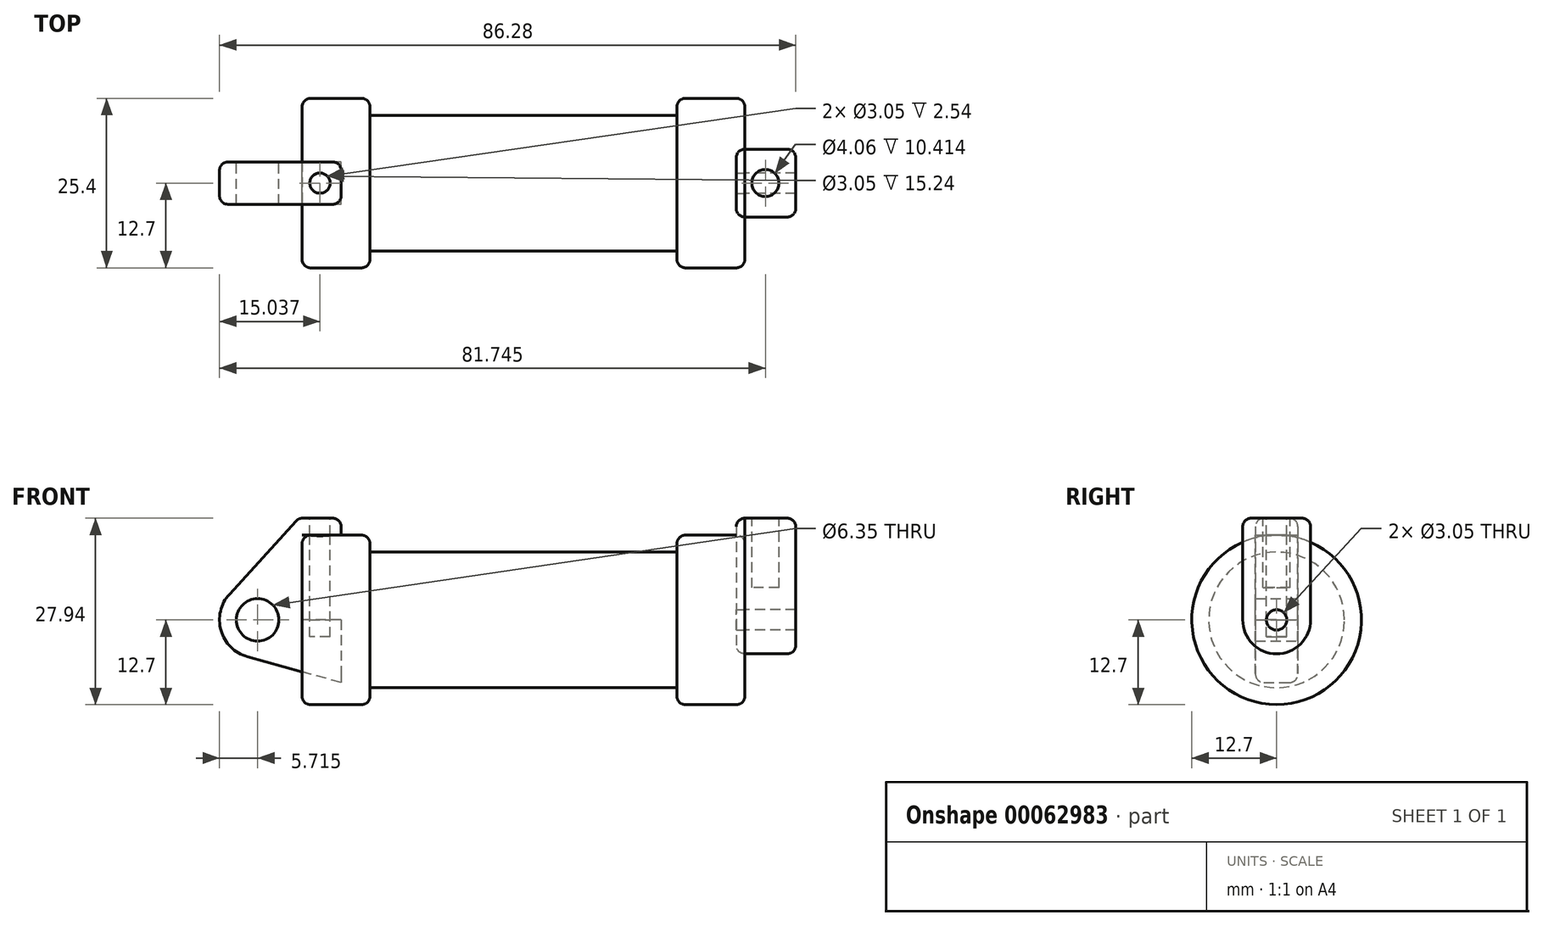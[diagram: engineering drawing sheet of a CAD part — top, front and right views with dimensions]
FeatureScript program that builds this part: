
annotation { "Feature Type Name" : "Feature", "Feature Type Description" : "" }
export const myFeature = defineFeature(function(context is Context, id is Id, definition is map)
    precondition{}
    {
        {
            var Q0;
            Q0=qCreatedBy(makeId("Front.planeOp"),FACE);
            var sketch = newSketch(context, id + "F0", { "sketchPlane" : qUnion([Q0])});
            skLineSegment(sketch, "E0", {"start": v(0, 0) * mm, "end": v(0, 12.7) * mm});
            skLineSegment(sketch, "E1", {"start": v(0, 12.7) * mm, "end": v(10.16, 12.7) * mm});
            skLineSegment(sketch, "E2", {"start": v(10.16, 12.7) * mm, "end": v(10.16, 10.16) * mm});
            skLineSegment(sketch, "E3", {"start": v(10.16, 10.16) * mm, "end": v(56.13, 10.16) * mm});
            skLineSegment(sketch, "E4", {"start": v(56.13, 10.16) * mm, "end": v(56.13, 12.7) * mm});
            skLineSegment(sketch, "E5", {"start": v(56.13, 12.7) * mm, "end": v(66.3, 12.7) * mm});
            skLineSegment(sketch, "E6", {"start": v(66.3, 12.7) * mm, "end": v(66.3, 0) * mm});
            skLineSegment(sketch, "E7", {"start": v(66.3, 0) * mm, "end": v(0, 0) * mm});
            skLineSegment(sketch, "E8", {"start": v(5.84, 15.24) * mm, "end": v(-0.5, 15.24) * mm});
            skLineSegment(sketch, "E9", {"start": v(-0.5, 15.24) * mm, "end": v(-10.88, 3.85) * mm});
            skLineSegment(sketch, "E10", {"start": v(0, 0) * mm, "end": v(-6.65, 0) * mm});
            skCircle(sketch, "E11", {"center": v(-6.65, 0) * mm, "radius": 5.72 * mm});
            skCircle(sketch, "E12", {"center": v(-6.65, 0) * mm, "radius": 3.18 * mm});
            skLineSegment(sketch, "E13", {"start": v(5.84, 15.24) * mm, "end": v(5.84, -9.4) * mm});
            skLineSegment(sketch, "E14", {"start": v(5.84, -9.4) * mm, "end": v(-8.18, -5.5) * mm});
            skSolve(sketch);
        }
        {
            var Q0;
            {var subQ0=sQuery(id+"F0.wireOp",EDGE,"E0");Q0=makeQuery(id+"F0.imprint","IMPRINT",FACE,{"disambiguationData":[TD([[makeQuery(id+"F0.imprint","IMPRINT",EDGE,{"derivedFrom":subQ0}),-1.0]])]});}
            var Q1;
            {var subQ0=sQuery(id+"F0.wireOp",EDGE,"E2");Q1=makeQuery(id+"F0.imprint","IMPRINT",FACE,{"disambiguationData":[TD([[makeQuery(id+"F0.imprint","IMPRINT",EDGE,{"derivedFrom":subQ0}),-1.0]])]});}
            var Q2;
            Q2=sQuery(id+"F0.wireOp",EDGE,"E7");
            revolve(context, id + "F1", {"entities" : qUnion([Q0, Q1]), "axis" : qUnion([Q2]), "revolveType" : RevolveType.FULL});
        }
        {
            var Q0;
            {var subQ3=sQuery(id+"F0.wireOp",EDGE,"E0");Q0=makeQuery(id+"F0.imprint","IMPRINT",FACE,{"disambiguationData":[TD([[makeQuery(id+"F0.imprint","IMPRINT",EDGE,{"derivedFrom":subQ3}),1.0]])]});}
            var Q1;
            {var subQ4=sQuery(id+"F0.wireOp",EDGE,"E12");Q1=makeQuery(id+"F0.imprint","IMPRINT",FACE,{"disambiguationData":[TD([[makeQuery(id+"F0.imprint","IMPRINT",EDGE,{"derivedFrom":subQ4}),-1.0]])]});}
            var Q2;
            {var subQ0=sQuery(id+"F0.wireOp",EDGE,"E14");Q2=makeQuery(id+"F0.imprint","IMPRINT",FACE,{"disambiguationData":[TD([[makeQuery(id+"F0.imprint","IMPRINT",EDGE,{"derivedFrom":subQ0}),-1.0]])]});}
            extrude(context, id + "F2", {"entities" : qUnion([Q0, Q1, Q2]), "endBound" : BoundingType.SYMMETRIC, "depth" : 6.35 * mm});
        }
        {
            var Q0;
            Q0=makeQuery(id+"F1.opRevolve","SWEPT_FACE",FACE,{"disambiguationData":[OSD([sQuery(id+"F0.wireOp",EDGE,"E6")])]});
            var sketch = newSketch(context, id + "F3", { "sketchPlane" : qUnion([Q0])});
            skCircle(sketch, "E15", {"center": v(0, 0) * mm, "radius": 1.52 * mm});
            skCircle(sketch, "E16", {"center": v(0, 0) * mm, "radius": 5.08 * mm});
            skLineSegment(sketch, "E17", {"start": v(-5.08, 0) * mm, "end": v(-5.08, 15.24) * mm});
            skLineSegment(sketch, "E18", {"start": v(-5.08, 15.24) * mm, "end": v(5.08, 15.24) * mm});
            skLineSegment(sketch, "E19", {"start": v(5.08, 15.24) * mm, "end": v(5.08, 0) * mm});
            skSolve(sketch);
        }
        {
            var Q0;
            {var subQ0=sQuery(id+"F3.wireOp",EDGE,"E18");Q0=makeQuery(id+"F3.imprint","IMPRINT",FACE,{"disambiguationData":[TD([[makeQuery(id+"F3.imprint","IMPRINT",EDGE,{"derivedFrom":subQ0}),-1.0]])]});}
            var Q1;
            {var subQ0=sQuery(id+"F3.wireOp",EDGE,"E17");var subQ1=sQuery(id+"F3.wireOp",EDGE,"E16");var subQ2=makeQuery(id+"F3.imprint","INTERSECT",VERTEX,{"derivedFrom":[subQ1,subQ0]});Q1=makeQuery(id+"F3.imprint","IMPRINT",FACE,{"disambiguationData":[TD([[makeQuery(id+"F3.imprint","IMPRINT",EDGE,{"disambiguationData":[TD([[subQ2,1.0]])],"derivedFrom":subQ1}),-1.0]])]});}
            var Q2;
            Q2=makeQuery(id+"F3.imprint","IMPRINT",FACE,{"disambiguationData":[TD([[makeQuery(id+"F3.imprint","IMPRINT",EDGE,{"derivedFrom":sQuery(id+"F3.wireOp",EDGE,"E15")}),-1.0]])]});
            extrude(context, id + "F4", {"entities" : qUnion([Q0, Q1, Q2]), "depth" : 7.62 * mm});
        }
        {
            var Q0;
            Q0 = qSketchRegion(id + "F3", true);
            extrude(context, id + "F5", {"entities" : qUnion([Q0]), "oppositeDirection" : true, "depth" : 1.27 * mm});
        }
        {
            var Q0;
            Q0=makeQuery(id+"F2.opExtrude","SWEPT_FACE",FACE,{"disambiguationData":[OSD([sQuery(id+"F0.wireOp",EDGE,"E8")])]});
            var sketch = newSketch(context, id + "F6", { "sketchPlane" : qUnion([Q0])});
            skCircle(sketch, "E20", {"center": v(2.67, 0) * mm, "radius": 1.52 * mm});
            skSolve(sketch);
        }
        {
            var Q0;
            Q0=makeQuery(id+"F6.imprint","IMPRINT",FACE,{"disambiguationData":[TD([[makeQuery(id+"F6.imprint","IMPRINT",EDGE,{"derivedFrom":sQuery(id+"F6.wireOp",EDGE,"E20")}),1.0]])]});
            extrude(context, id + "F7", {"entities" : qUnion([Q0]), "operationType" : NewBodyOperationType.REMOVE, "oppositeDirection" : true, "depth" : 17.78 * mm});
        }
        {
            var Q0;
            Q0=makeQuery(id+"F4.opExtrude","SWEPT_FACE",FACE,{"disambiguationData":[OSD([sQuery(id+"F3.wireOp",EDGE,"E18")])]});
            var sketch = newSketch(context, id + "F8", { "sketchPlane" : qUnion([Q0])});
            skCircle(sketch, "E21", {"center": v(69.38, 0) * mm, "radius": 2.03 * mm});
            skLineSegment(sketch, "E22", {"start": v(64.84, 0) * mm, "end": v(73.91, 0) * mm, "construction": true});
            skLineSegment(sketch, "E23", {"start": v(69.38, 5.08) * mm, "end": v(69.38, -5.08) * mm, "construction": true});
            skSolve(sketch);
        }
        {
            var Q0;
            Q0=makeQuery(id+"F8.imprint","IMPRINT",FACE,{"disambiguationData":[TD([[makeQuery(id+"F8.imprint","IMPRINT",EDGE,{"derivedFrom":sQuery(id+"F8.wireOp",EDGE,"E21")}),1.0]])]});
            var Q1;
            Q1=sQuery(id+"F8.wireOp",EDGE,"E21");
            extrude(context, id + "F9", {"entities" : qUnion([Q0]), "operationType" : NewBodyOperationType.REMOVE, "surfaceEntities" : qUnion([Q1]), "oppositeDirection" : true, "depth" : 10.4 * mm});
        }
        {
            var Q0;
            Q0=makeQuery(id+"F4.opExtrude","CAP_EDGE",EDGE,{"disambiguationData":[OSD([sQuery(id+"F3.wireOp",EDGE,"E18")])],"isStart":false});
            var Q1;
            Q1=makeQuery(id+"F4.opExtrude","SWEPT_EDGE",EDGE,{"disambiguationData":[OSD([sQuery(id+"F3.wireOp",EDGE,"E17"),sQuery(id+"F3.wireOp",EDGE,"E18")])]});
            var Q2;
            Q2=makeQuery(id+"F4.opExtrude","SWEPT_EDGE",EDGE,{"disambiguationData":[OSD([sQuery(id+"F3.wireOp",EDGE,"E18"),sQuery(id+"F3.wireOp",EDGE,"E19")])]});
            var Q3;
            Q3=makeQuery(id+"F4.opExtrude","CAP_EDGE",EDGE,{"disambiguationData":[OSD([sQuery(id+"F3.wireOp",EDGE,"E17")])],"isStart":false});
            var Q4;
            Q4=makeQuery(id+"F4.opExtrude","CAP_EDGE",EDGE,{"disambiguationData":[OSD([sQuery(id+"F3.wireOp",EDGE,"E19")])],"isStart":false});
            var Q5;
            Q5=makeQuery(id+"F4.opExtrude","CAP_EDGE",EDGE,{"disambiguationData":[OSD([sQuery(id+"F3.wireOp",EDGE,"E16")])],"isStart":false});
            var Q6;
            Q6=makeQuery(id+"F1.opRevolve","SWEPT_EDGE",EDGE,{"disambiguationData":[OSD([sQuery(id+"F0.wireOp",EDGE,"E5"),sQuery(id+"F0.wireOp",EDGE,"E6")])]});
            var Q7;
            Q7=makeQuery(id+"F1.opRevolve","SWEPT_EDGE",EDGE,{"disambiguationData":[OSD([sQuery(id+"F0.wireOp",EDGE,"E4"),sQuery(id+"F0.wireOp",EDGE,"E5")])]});
            var Q8;
            Q8=makeQuery(id+"F1.opRevolve","SWEPT_EDGE",EDGE,{"disambiguationData":[OSD([sQuery(id+"F0.wireOp",EDGE,"E1"),sQuery(id+"F0.wireOp",EDGE,"E2")])]});
            var Q9;
            Q9=makeQuery(id+"F1.opRevolve","SWEPT_EDGE",EDGE,{"disambiguationData":[OSD([sQuery(id+"F0.wireOp",EDGE,"E0"),sQuery(id+"F0.wireOp",EDGE,"E1")])]});
            var Q10;
            Q10=makeQuery(id+"F2.opExtrude","CAP_EDGE",EDGE,{"disambiguationData":[OSD([sQuery(id+"F0.wireOp",EDGE,"E9")])],"isStart":true});
            var Q11;
            Q11=makeQuery(id+"F2.opExtrude","CAP_EDGE",EDGE,{"disambiguationData":[OSD([sQuery(id+"F0.wireOp",EDGE,"E11")])],"isStart":true});
            var Q12;
            Q12=makeQuery(id+"F2.opExtrude","CAP_EDGE",EDGE,{"disambiguationData":[OSD([sQuery(id+"F0.wireOp",EDGE,"E14")])],"isStart":true});
            var Q13;
            Q13=makeQuery(id+"F2.opExtrude","CAP_EDGE",EDGE,{"disambiguationData":[OSD([sQuery(id+"F0.wireOp",EDGE,"E9")])],"isStart":false});
            var Q14;
            Q14=makeQuery(id+"F2.opExtrude","CAP_EDGE",EDGE,{"disambiguationData":[OSD([sQuery(id+"F0.wireOp",EDGE,"E11")])],"isStart":false});
            var Q15;
            Q15=makeQuery(id+"F2.opExtrude","CAP_EDGE",EDGE,{"disambiguationData":[OSD([sQuery(id+"F0.wireOp",EDGE,"E14")])],"isStart":false});
            var Q16;
            Q16=makeQuery(id+"F2.opExtrude","CAP_EDGE",EDGE,{"disambiguationData":[OSD([sQuery(id+"F0.wireOp",EDGE,"E8")])],"isStart":true});
            var Q17;
            Q17=makeQuery(id+"F2.opExtrude","SWEPT_EDGE",EDGE,{"disambiguationData":[OSD([sQuery(id+"F0.wireOp",EDGE,"E8"),sQuery(id+"F0.wireOp",EDGE,"E13")])]});
            var Q18;
            Q18=makeQuery(id+"F2.opExtrude","CAP_EDGE",EDGE,{"disambiguationData":[OSD([sQuery(id+"F0.wireOp",EDGE,"E8")])],"isStart":false});
            var Q19;
            Q19=makeQuery(id+"F2.opExtrude","SWEPT_EDGE",EDGE,{"disambiguationData":[OSD([sQuery(id+"F0.wireOp",EDGE,"E8"),sQuery(id+"F0.wireOp",EDGE,"E9")])]});
            var Q20;
            {var subQ0=sQuery(id+"F0.wireOp",EDGE,"E13");Q20=makeQuery(id+"F2.opExtrude","CAP_EDGE",EDGE,{"disambiguationData":[OSD([subQ0]),TDD([makeQuery(id+"F0.imprint","IMPRINT",EDGE,{"disambiguationData":[TD([[makeQuery(id+"F0.imprint","INTERSECT",VERTEX,{"derivedFrom":[sQuery(id+"F0.wireOp",EDGE,"E8"),subQ0]}),-1.0]])],"derivedFrom":subQ0})])],"isStart":true});}
            var Q21;
            {var subQ0=sQuery(id+"F0.wireOp",EDGE,"E13");Q21=makeQuery(id+"F2.opExtrude","CAP_EDGE",EDGE,{"disambiguationData":[OSD([subQ0]),TDD([makeQuery(id+"F0.imprint","IMPRINT",EDGE,{"disambiguationData":[TD([[makeQuery(id+"F0.imprint","INTERSECT",VERTEX,{"derivedFrom":[sQuery(id+"F0.wireOp",EDGE,"E8"),subQ0]}),-1.0]])],"derivedFrom":subQ0})])],"isStart":false});}
            var Q22;
            Q22=makeQuery(id+"F5.opExtrude","CAP_EDGE",EDGE,{"disambiguationData":[OSD([sQuery(id+"F3.wireOp",EDGE,"E18")])],"isStart":false});
            var Q23;
            Q23=makeQuery(id+"F5.opExtrude","SWEPT_EDGE",EDGE,{"disambiguationData":[OSD([sQuery(id+"F3.wireOp",EDGE,"E18"),sQuery(id+"F3.wireOp",EDGE,"E19")])]});
            var Q24;
            Q24=makeQuery(id+"F5.opExtrude","SWEPT_EDGE",EDGE,{"disambiguationData":[OSD([sQuery(id+"F3.wireOp",EDGE,"E17"),sQuery(id+"F3.wireOp",EDGE,"E18")])]});
            var Q25;
            Q25=makeQuery(id+"F5.opExtrude","CAP_EDGE",EDGE,{"disambiguationData":[OSD([sQuery(id+"F3.wireOp",EDGE,"E17")])],"isStart":false});
            var Q26;
            Q26=makeQuery(id+"F5.opExtrude","CAP_EDGE",EDGE,{"disambiguationData":[OSD([sQuery(id+"F3.wireOp",EDGE,"E19")])],"isStart":false});
            fillet(context, id + "F10", {"entities" : qUnion([Q0, Q1, Q2, Q3, Q4, Q5, Q6, Q7, Q8, Q9, Q10, Q11, Q12, Q13, Q14, Q15, Q16, Q17, Q18, Q19, Q20, Q21, Q22, Q23, Q24, Q25, Q26]), "radius" : 1.27 * mm, "tangentPropagation" : true, "allowEdgeOverflow" : false});
        }
    });
